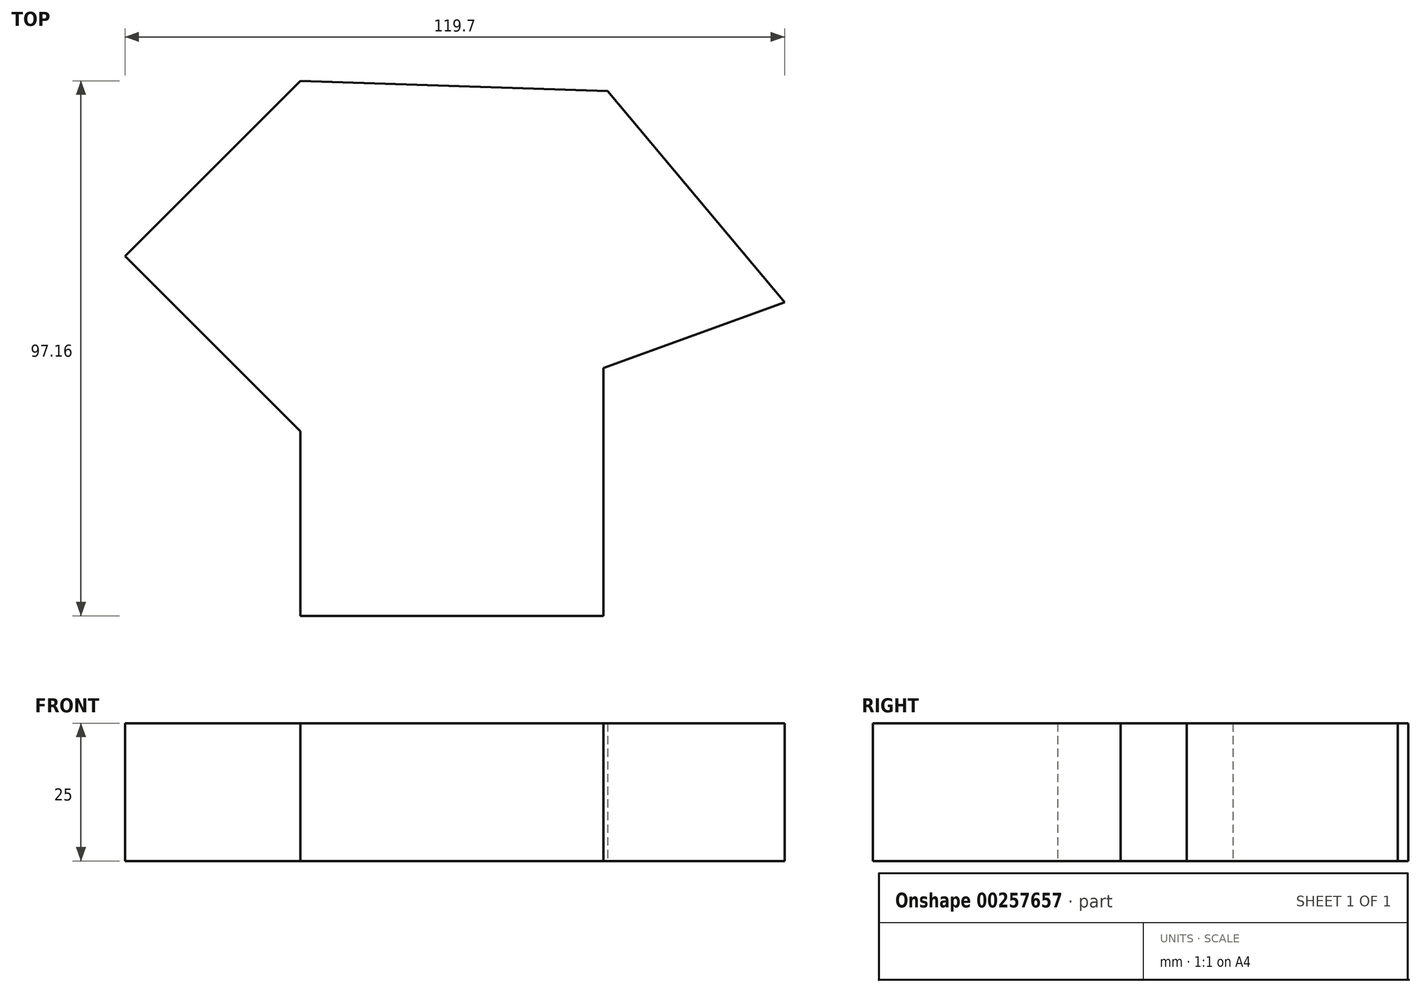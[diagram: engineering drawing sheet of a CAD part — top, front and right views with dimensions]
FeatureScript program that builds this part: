
annotation { "Feature Type Name" : "Feature", "Feature Type Description" : "" }
export const myFeature = defineFeature(function(context is Context, id is Id, definition is map)
    precondition{}
    {
        {
            var Q0;
            Q0=qCreatedBy(makeId("Top.planeOp"),FACE);
            var sketch = newSketch(context, id + "F0", { "sketchPlane" : qUnion([Q0])});
            skLineSegment(sketch, "E0", {"start": v(25.58, 25.51) * mm, "end": v(57.72, -12.79) * mm});
            skLineSegment(sketch, "E1", {"start": v(57.72, -12.79) * mm, "end": v(24.84, -24.76) * mm});
            skLineSegment(sketch, "E2", {"start": v(24.84, -24.76) * mm, "end": v(24.84, -69.76) * mm});
            skLineSegment(sketch, "E3", {"start": v(24.84, -69.76) * mm, "end": v(-30.16, -69.76) * mm});
            skLineSegment(sketch, "E4", {"start": v(-30.16, -69.76) * mm, "end": v(-30.16, -36.24) * mm});
            skLineSegment(sketch, "E5", {"start": v(-30.16, -36.24) * mm, "end": v(-61.98, -4.42) * mm});
            skLineSegment(sketch, "E6", {"start": v(-30.16, 27.4) * mm, "end": v(-61.98, -4.42) * mm});
            skLineSegment(sketch, "E7", {"start": v(-61.98, -4.42) * mm, "end": v(-28.85, -4.42) * mm});
            skLineSegment(sketch, "E8", {"start": v(57.72, -12.79) * mm, "end": v(39.06, -12.79) * mm});
            skLineSegment(sketch, "E9", {"start": v(-30.16, 27.4) * mm, "end": v(25.58, 25.51) * mm});
            skSolve(sketch);
        }
        {
            var Q0;
            Q0 = qSketchRegion(id + "F0", true);
            extrude(context, id + "F1", {"entities" : qUnion([Q0]), "depth" : 25 * mm});
        }
    });
